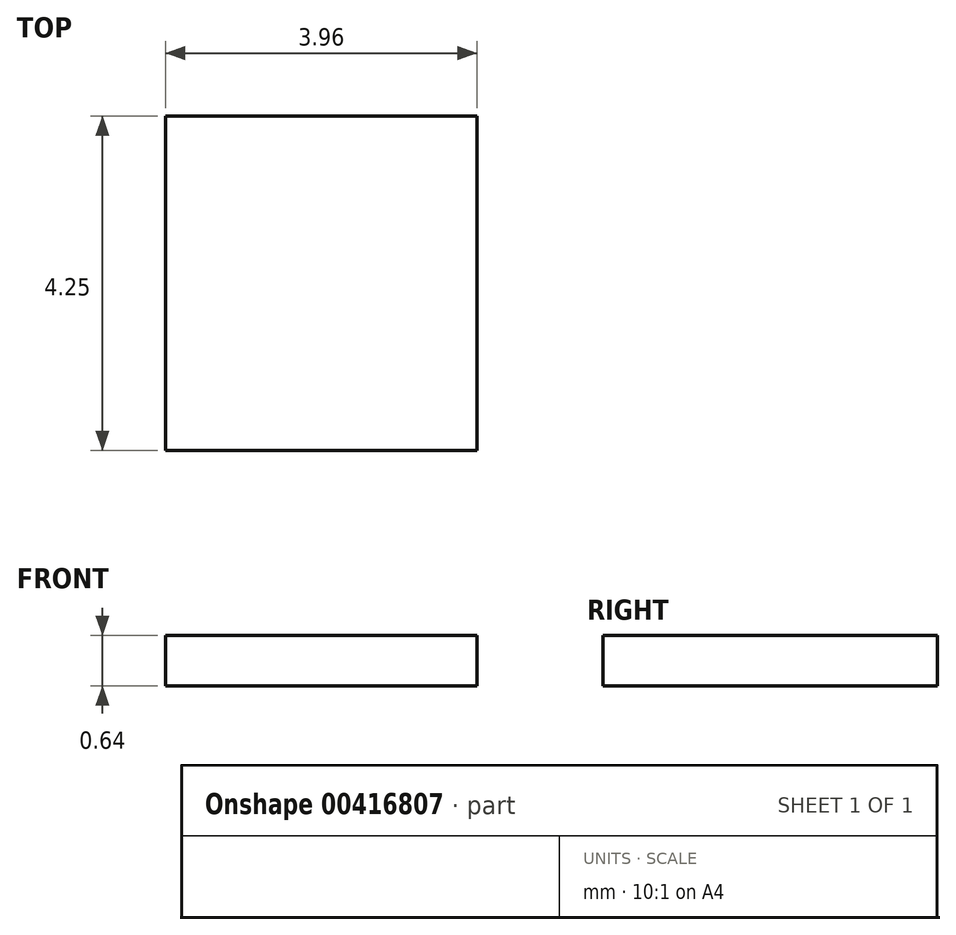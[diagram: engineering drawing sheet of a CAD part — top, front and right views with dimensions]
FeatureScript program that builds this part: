
annotation { "Feature Type Name" : "Feature", "Feature Type Description" : "" }
export const myFeature = defineFeature(function(context is Context, id is Id, definition is map)
    precondition{}
    {
        {
            var Q0;
            Q0=qCreatedBy(makeId("Top.planeOp"),FACE);
            var sketch = newSketch(context, id + "F0", { "sketchPlane" : qUnion([Q0])});
            skLineSegment(sketch, "E0.bottom", {"start": v(0, 0) * mm, "end": v(3.96, 0) * mm});
            skLineSegment(sketch, "E0.top", {"start": v(0, 4.25) * mm, "end": v(3.96, 4.25) * mm});
            skLineSegment(sketch, "E0.left", {"start": v(0, 0) * mm, "end": v(0, 4.25) * mm});
            skLineSegment(sketch, "E0.right", {"start": v(3.96, 0) * mm, "end": v(3.96, 4.25) * mm});
            skSolve(sketch);
        }
        {
            var Q0;
            Q0 = qSketchRegion(id + "F0", true);
            extrude(context, id + "F1", {"entities" : qUnion([Q0]), "depth" : .64 * mm, "offsetDistance" : 25.4 * mm});
        }
    });
